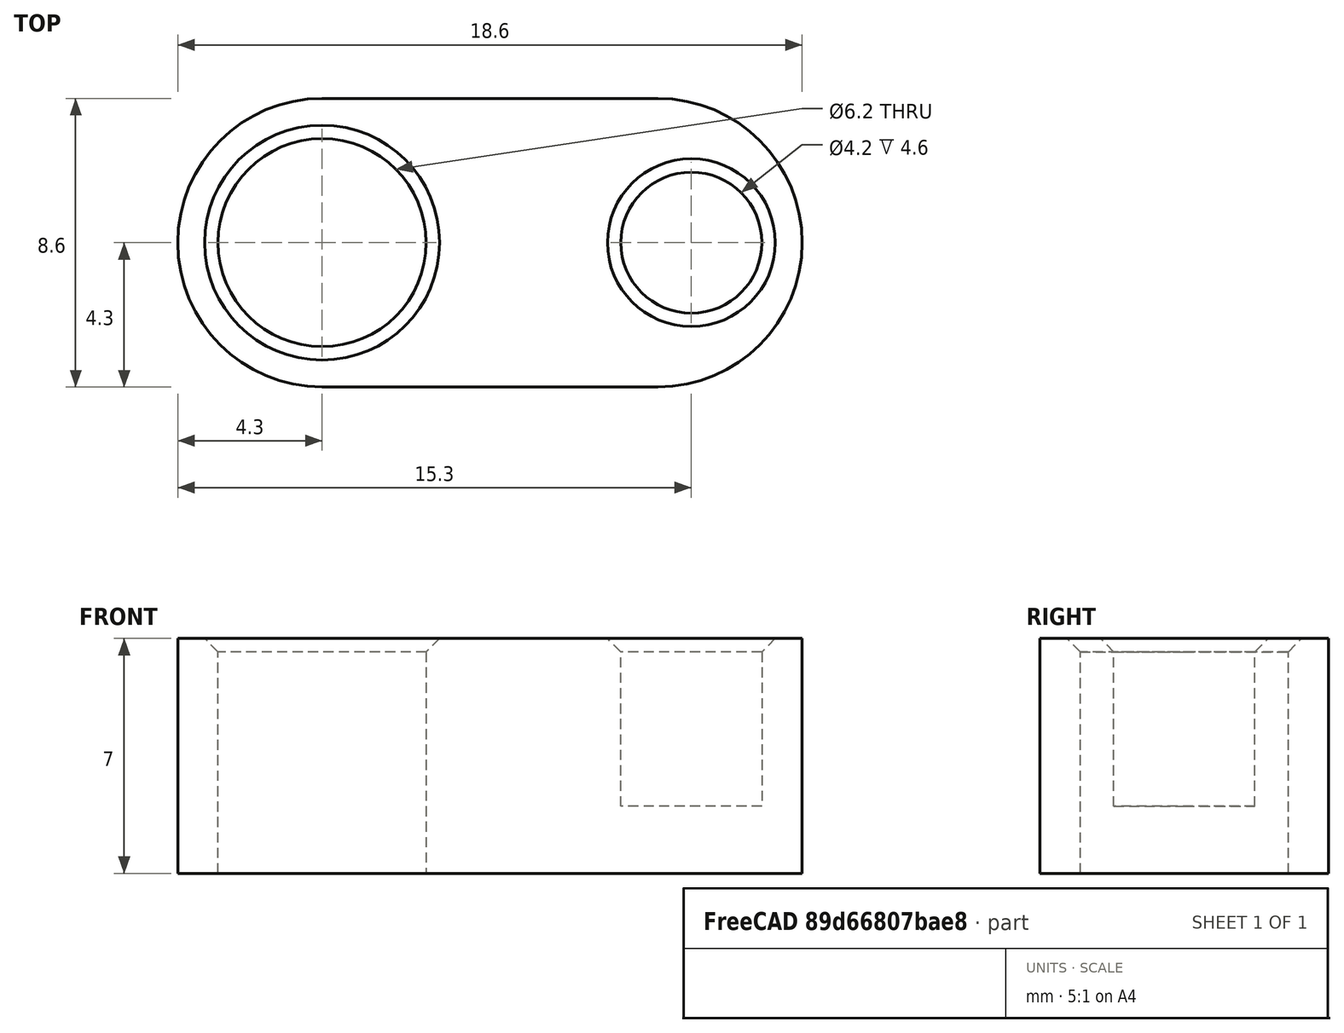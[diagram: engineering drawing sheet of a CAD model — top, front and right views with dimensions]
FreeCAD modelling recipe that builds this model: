
FCSTD DOCUMENT  (FreeCAD 0.21R33771 (Git))
Label: J-Pole_433_Spacer
Comment: J-Pole antenna spacer for the matching part
License: CC BY-SA 4.0 (SPDX-ID: CC-BY-SA-4.0)
LicenseURL: https://creativecommons.org/licenses/by-sa/4.0/legalcode.txt
objects: Sketcher::SketchObject×3, PartDesign::Pocket×2, PartDesign::Pad×1, PartDesign::Fillet×1, PartDesign::Chamfer×1, PartDesign::Body×1, Mesh::Feature×1
note: 14 computed .brp shape members not serialized (recipe doc carries the construction recipe); baked Part::Feature solids carry a one-line shape summary decoded from their .brp

FEATURE [Sketcher::SketchObject] Sketch
  FullyConstrained = true
  MapMode = 5
  Support = -> [XY_Plane]
  sketch-geometry (4):
    g0: LineSegment StartX=-9.3 StartY=4.3 StartZ=0 EndX=9.3 EndY=4.3 EndZ=0
    g1: LineSegment StartX=9.3 StartY=4.3 StartZ=0 EndX=9.3 EndY=-4.3 EndZ=0
    g2: LineSegment StartX=9.3 StartY=-4.3 StartZ=0 EndX=-9.3 EndY=-4.3 EndZ=0
    g3: LineSegment StartX=-9.3 StartY=-4.3 StartZ=0 EndX=-9.3 EndY=4.3 EndZ=0
  constraints (11):
    c: Coincident(g0,g1)
    c: Coincident(g1,g2)
    c: Coincident(g2,g3)
    c: Coincident(g3,g0)
    c: Horizontal(g0)
    c: Horizontal(g2)
    c: Vertical(g1)
    c: Vertical(g3)
    c: DistanceY(g3,g3) = 8.6
    c: DistanceX(g0,g0) = 18.6
    c: Symmetric(g0,g1,g-1)
FEATURE [PartDesign::Pad] Pad
  Direction = (0,0,1)
  Length = 7
  Length2 = 10
  Profile = -> Sketch
  ReferenceAxis = -> Sketch [N_Axis]
  Type = 0
FEATURE [Sketcher::SketchObject] Sketch001
  ExternalGeometry = -> [Pad]
  FullyConstrained = true
  MapMode = 5
  Placement = pos=(0,0,7) rot=(0,0,1;0rad)
  Support = -> [Pad]
  sketch-geometry (1):
    g0: Circle CenterX=-5 CenterY=0 CenterZ=0 NormalX=0 NormalY=0 NormalZ=1 AngleXU=0 Radius=3.1
  constraints (3):
    c: PointOnObject(g0,g-1)
    c: Radius(g0) = 3.1
    c: Distance(g0,g-3) = 1.2
FEATURE [PartDesign::Pocket] Pocket
  BaseFeature = -> Pad
  Direction = (0,0,-1)
  Length = 5
  Length2 = 5
  Profile = -> Sketch001
  ReferenceAxis = -> Sketch001 [N_Axis]
  Type = 1
FEATURE [Sketcher::SketchObject] Sketch002
  ExternalGeometry = -> [Pocket]
  FullyConstrained = true
  MapMode = 5
  Placement = pos=(0,0,7) rot=(0,0,1;0rad)
  Support = -> [Pocket]
  sketch-geometry (1):
    g0: Circle CenterX=6 CenterY=0 CenterZ=0 NormalX=0 NormalY=0 NormalZ=1 AngleXU=0 Radius=2.1
  constraints (3):
    c: PointOnObject(g0,g-1)
    c: Radius(g0) = 2.1
    c: Distance(g0,g-3) = 1.2
FEATURE [PartDesign::Pocket] Pocket001
  BaseFeature = -> Pocket
  Direction = (0,0,-1)
  Length = 5
  Length2 = 5
  Profile = -> Sketch002
  ReferenceAxis = -> Sketch002 [N_Axis]
  Type = 0
FEATURE [PartDesign::Fillet] Fillet
  Base = -> Pocket001 [Edge1,Edge5,Edge2,Edge8]
  BaseFeature = -> Pocket001
  Radius = 4.299
  SupportTransform = false
  UseAllEdges = false
FEATURE [PartDesign::Chamfer] Chamfer
  Angle = 45
  Base = -> Fillet [Edge22,Edge23]
  BaseFeature = -> Fillet
  ChamferType = 0
  FlipDirection = false
  Size = 0.4
  Size2 = 1
  SupportTransform = false
  UseAllEdges = false
FEATURE [PartDesign::Body] Body
  Group = -> [Sketch,Pad,Sketch001,Pocket,Sketch002,Pocket001,Fillet,Chamfer]
  Origin = -> Origin
  Tip = -> Chamfer
FEATURE [Mesh::Feature] Mesh  label="J-Pole_433_Spacer"
